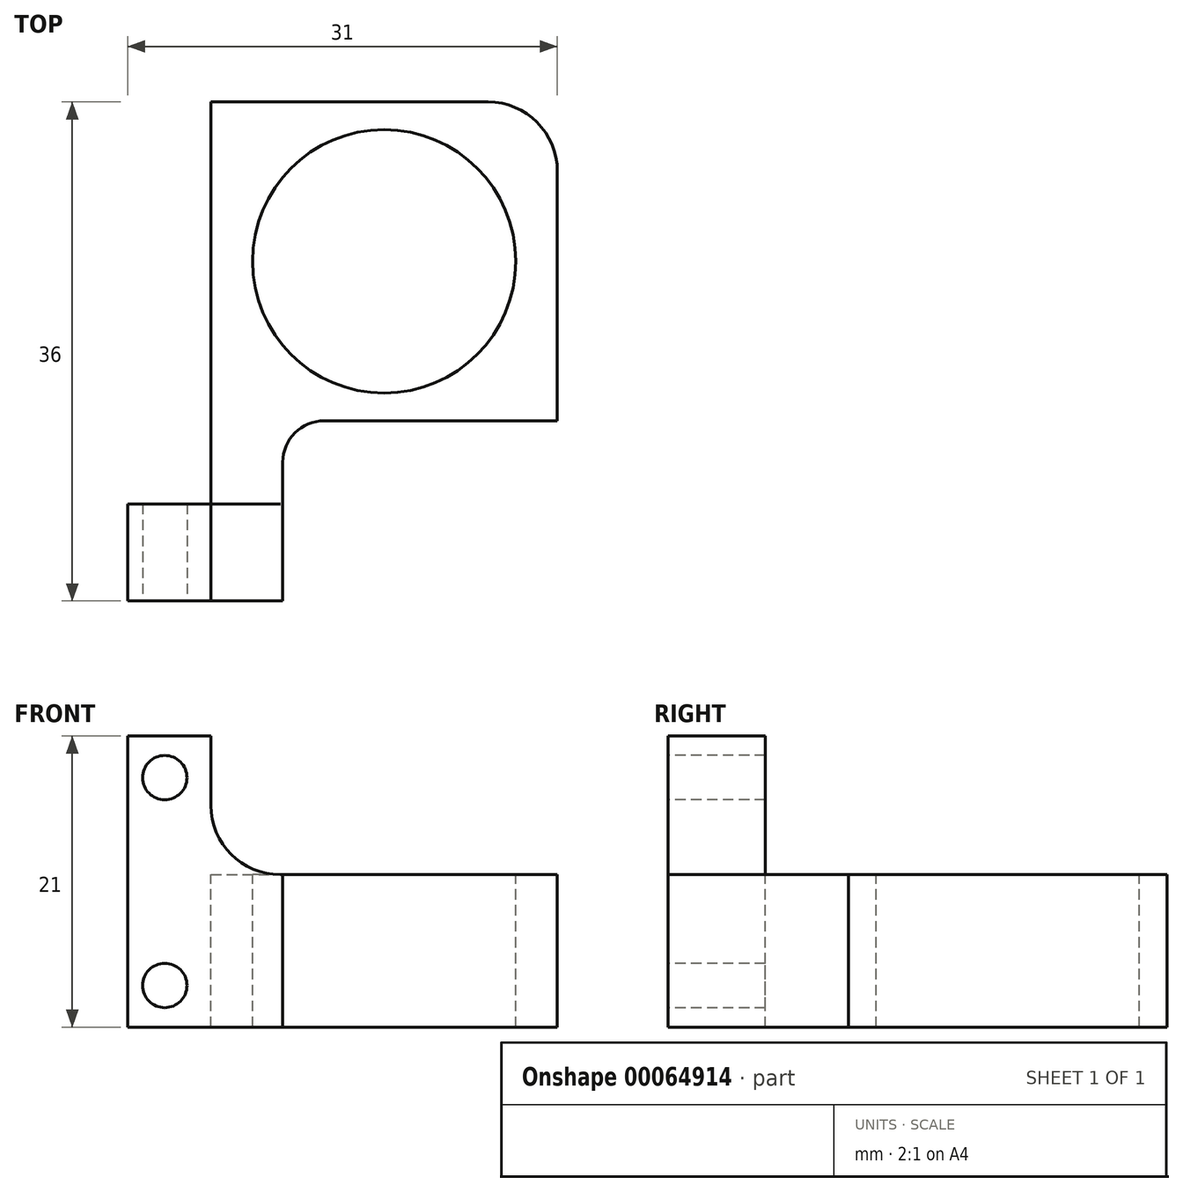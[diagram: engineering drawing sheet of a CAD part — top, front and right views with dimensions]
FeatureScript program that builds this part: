
annotation { "Feature Type Name" : "Feature", "Feature Type Description" : "" }
export const myFeature = defineFeature(function(context is Context, id is Id, definition is map)
    precondition{}
    {
        {
            var Q0;
            Q0=qCreatedBy(makeId("Top.planeOp"),FACE);
            var sketch = newSketch(context, id + "F0", { "sketchPlane" : qUnion([Q0])});
            skLineSegment(sketch, "E0.bottom", {"start": v(0, 0) * mm, "end": v(31, 0) * mm});
            skLineSegment(sketch, "E0.top", {"start": v(0, 36) * mm, "end": v(31, 36) * mm});
            skLineSegment(sketch, "E0.left", {"start": v(0, 0) * mm, "end": v(0, 36) * mm});
            skLineSegment(sketch, "E0.right", {"start": v(31, 0) * mm, "end": v(31, 36) * mm});
            skSolve(sketch);
        }
        {
            var Q0;
            Q0=qSketchRegion(id+"F0",true);
            extrude(context, id + "F1", {"entities" : qUnion([Q0]), "depth" : 4 * mm});
        }
        {
            var Q0;
            Q0=makeQuery(id+"F1.opExtrude","CAP_FACE",FACE,{"disambiguationData":[OSD([sQuery(id+"F0.wireOp",EDGE,"E0.bottom"),sQuery(id+"F0.wireOp",EDGE,"E0.top"),sQuery(id+"F0.wireOp",EDGE,"E0.left"),sQuery(id+"F0.wireOp",EDGE,"E0.right")])],"isStart":false});
            var sketch = newSketch(context, id + "F2", { "sketchPlane" : qUnion([Q0])});
            skCircle(sketch, "E1", {"center": v(18.5, 24.5) * mm, "radius": 9.5 * mm});
            skLineSegment(sketch, "E2.bottom", {"start": v(0, 36) * mm, "end": v(6, 36) * mm});
            skLineSegment(sketch, "E2.top", {"start": v(0, 7) * mm, "end": v(6, 7) * mm});
            skLineSegment(sketch, "E2.left", {"start": v(0, 36) * mm, "end": v(0, 7) * mm});
            skLineSegment(sketch, "E2.right", {"start": v(6, 36) * mm, "end": v(6, 7) * mm});
            skLineSegment(sketch, "E3.bottom", {"start": v(31, 0) * mm, "end": v(11.18, 0) * mm});
            skLineSegment(sketch, "E3.top", {"start": v(31, 13) * mm, "end": v(11.18, 13) * mm});
            skLineSegment(sketch, "E3.left", {"start": v(31, 0) * mm, "end": v(31, 13) * mm});
            skLineSegment(sketch, "E3.right", {"start": v(11.18, 0) * mm, "end": v(11.18, 13) * mm});
            skSolve(sketch);
        }
        {
            var Q0;
            Q0=qSketchRegion(id+"F2",true);
            extrude(context, id + "F3", {"entities" : qUnion([Q0]), "operationType" : NewBodyOperationType.REMOVE, "oppositeDirection" : true, "depth" : 25 * mm});
        }
        {
            var Q0;
            Q0=makeQuery(id+"F1.opExtrude","CAP_FACE",FACE,{"disambiguationData":[OSD([sQuery(id+"F0.wireOp",EDGE,"E0.bottom"),sQuery(id+"F0.wireOp",EDGE,"E0.top"),sQuery(id+"F0.wireOp",EDGE,"E0.left"),sQuery(id+"F0.wireOp",EDGE,"E0.right")])],"isStart":false});
            var sketch = newSketch(context, id + "F4", { "sketchPlane" : qUnion([Q0])});
            skLineSegment(sketch, "E4.bottom", {"start": v(0, 7) * mm, "end": v(6, 7) * mm});
            skLineSegment(sketch, "E4.top", {"start": v(0, 0) * mm, "end": v(6, 0) * mm});
            skLineSegment(sketch, "E4.left", {"start": v(0, 7) * mm, "end": v(0, 0) * mm});
            skLineSegment(sketch, "E4.right", {"start": v(6, 7) * mm, "end": v(6, 0) * mm});
            skSolve(sketch);
        }
        {
            var Q0;
            Q0=qSketchRegion(id+"F4",true);
            var Q1;
            {var subQ1=sQuery(id+"F4.wireOp",EDGE,"E4.right");Q1=makeQuery(id+"F4.imprint","IMPRINT",FACE,{"disambiguationData":[TD([[makeQuery(id+"F4.imprint","IMPRINT",EDGE,{"derivedFrom":subQ1}),1.0]])]});}
            extrude(context, id + "F5", {"entities" : qUnion([Q0, Q1]), "operationType" : NewBodyOperationType.ADD, "depth" : 7 * mm});
        }
        {
            var Q0;
            Q0=makeQuery(id+"F4.imprint","IMPRINT",FACE,{"disambiguationData":[TD([[makeQuery(id+"F4.imprint","IMPRINT",EDGE,{"derivedFrom":sQuery(id+"F4.wireOp",EDGE,"E4.bottom")}),-1.0]])]});
            extrude(context, id + "F6", {"entities" : qUnion([Q0]), "operationType" : NewBodyOperationType.ADD, "depth" : 17 * mm});
        }
        {
            var Q0;
            Q0=makeQuery(id+"F5.boolean.opBoolean","MERGE",FACE,{"derivedFrom":[makeQuery(id+"F1.opExtrude","SWEPT_FACE",FACE,{"disambiguationData":[OSD([sQuery(id+"F0.wireOp",EDGE,"E0.bottom")])]}),makeQuery(id+"F5.opExtrude","SWEPT_FACE",FACE,{"disambiguationData":[OSD([sQuery(id+"F4.wireOp",EDGE,"E4.top")])]})]});
            var sketch = newSketch(context, id + "F7", { "sketchPlane" : qUnion([Q0])});
            skLineSegment(sketch, "E5", {"start": v(2.68, 18) * mm, "end": v(2.68, 3) * mm});
            skCircle(sketch, "E6", {"center": v(2.68, 18) * mm, "radius": 1.6 * mm});
            skCircle(sketch, "E7", {"center": v(2.68, 3) * mm, "radius": 1.6 * mm});
            skSolve(sketch);
        }
        {
            var Q0;
            Q0=qSketchRegion(id+"F7",true);
            extrude(context, id + "F8", {"entities" : qUnion([Q0]), "operationType" : NewBodyOperationType.REMOVE, "oppositeDirection" : true, "depth" : 25 * mm});
        }
        {
            var Q0;
            Q0=makeQuery(id+"F1.opExtrude","SWEPT_EDGE",EDGE,{"disambiguationData":[OSD([sQuery(id+"F0.wireOp",EDGE,"E0.bottom"),sQuery(id+"F0.wireOp",EDGE,"E0.right")])]});
            var Q1;
            Q1=makeQuery(id+"F1.opExtrude","SWEPT_EDGE",EDGE,{"disambiguationData":[OSD([sQuery(id+"F0.wireOp",EDGE,"E0.top"),sQuery(id+"F0.wireOp",EDGE,"E0.right")])]});
            var Q2;
            Q2=makeQuery(id+"F3.boolean.opBoolean","COPY",EDGE,{"derivedFrom":makeQuery(id+"F3.opExtrude","SWEPT_EDGE",EDGE,{"disambiguationData":[OSD([sQuery(id+"F0.wireOp",EDGE,"E0.top"),sQuery(id+"F2.wireOp",EDGE,"E2.bottom"),sQuery(id+"F2.wireOp",EDGE,"E2.right")])]})});
            var Q3;
            Q3=makeQuery(id+"F3.boolean.opBoolean","COPY",EDGE,{"derivedFrom":makeQuery(id+"F3.opExtrude","SWEPT_EDGE",EDGE,{"disambiguationData":[OSD([sQuery(id+"F0.wireOp",EDGE,"E0.right"),sQuery(id+"F2.wireOp",EDGE,"E3.top"),sQuery(id+"F2.wireOp",EDGE,"E3.left")])]})});
            fillet(context, id + "F9", {"entities" : qUnion([Q0, Q1, Q2, Q3]), "radius" : 5 * mm, "tangentPropagation" : true, "allowEdgeOverflow" : false});
        }
        {
            var Q0;
            {var subQ0=sQuery(id+"F2.wireOp",EDGE,"E3.top");var subQ1=sQuery(id+"F2.wireOp",EDGE,"E3.right");Q0=makeQuery(id+"F5.boolean.opBoolean","MERGE",EDGE,{"derivedFrom":[makeQuery(id+"F3.boolean.opBoolean","COPY",EDGE,{"derivedFrom":makeQuery(id+"F3.opExtrude","SWEPT_EDGE",EDGE,{"disambiguationData":[OSD([subQ0,subQ1])]})}),makeQuery(id+"F5.opExtrude","SWEPT_EDGE",EDGE,{"disambiguationData":[OSD([subQ0,subQ1])]})]});}
            fillet(context, id + "F10", {"entities" : qUnion([Q0]), "radius" : 3 * mm, "tangentPropagation" : true, "allowEdgeOverflow" : false});
        }
        {
            var Q0;
            Q0=makeQuery(id+"F6.boolean.opBoolean","INTERSECT",EDGE,{"derivedFrom":[makeQuery(id+"F5.opExtrude","CAP_FACE",FACE,{"disambiguationData":[OSD([sQuery(id+"F0.wireOp",EDGE,"E0.bottom"),sQuery(id+"F0.wireOp",EDGE,"E0.top"),sQuery(id+"F0.wireOp",EDGE,"E0.right"),sQuery(id+"F2.wireOp",EDGE,"E1"),sQuery(id+"F2.wireOp",EDGE,"E2.right"),sQuery(id+"F2.wireOp",EDGE,"E3.top"),sQuery(id+"F2.wireOp",EDGE,"E3.right"),sQuery(id+"F4.wireOp",EDGE,"E4.bottom"),sQuery(id+"F4.wireOp",EDGE,"E4.top"),sQuery(id+"F4.wireOp",EDGE,"E4.left")])],"isStart":false}),makeQuery(id+"F6.opExtrude","SWEPT_FACE",FACE,{"disambiguationData":[OSD([sQuery(id+"F4.wireOp",EDGE,"E4.right")])]})]});
            fillet(context, id + "F11", {"entities" : qUnion([Q0]), "radius" : 5 * mm, "tangentPropagation" : true, "allowEdgeOverflow" : false});
        }
    });
